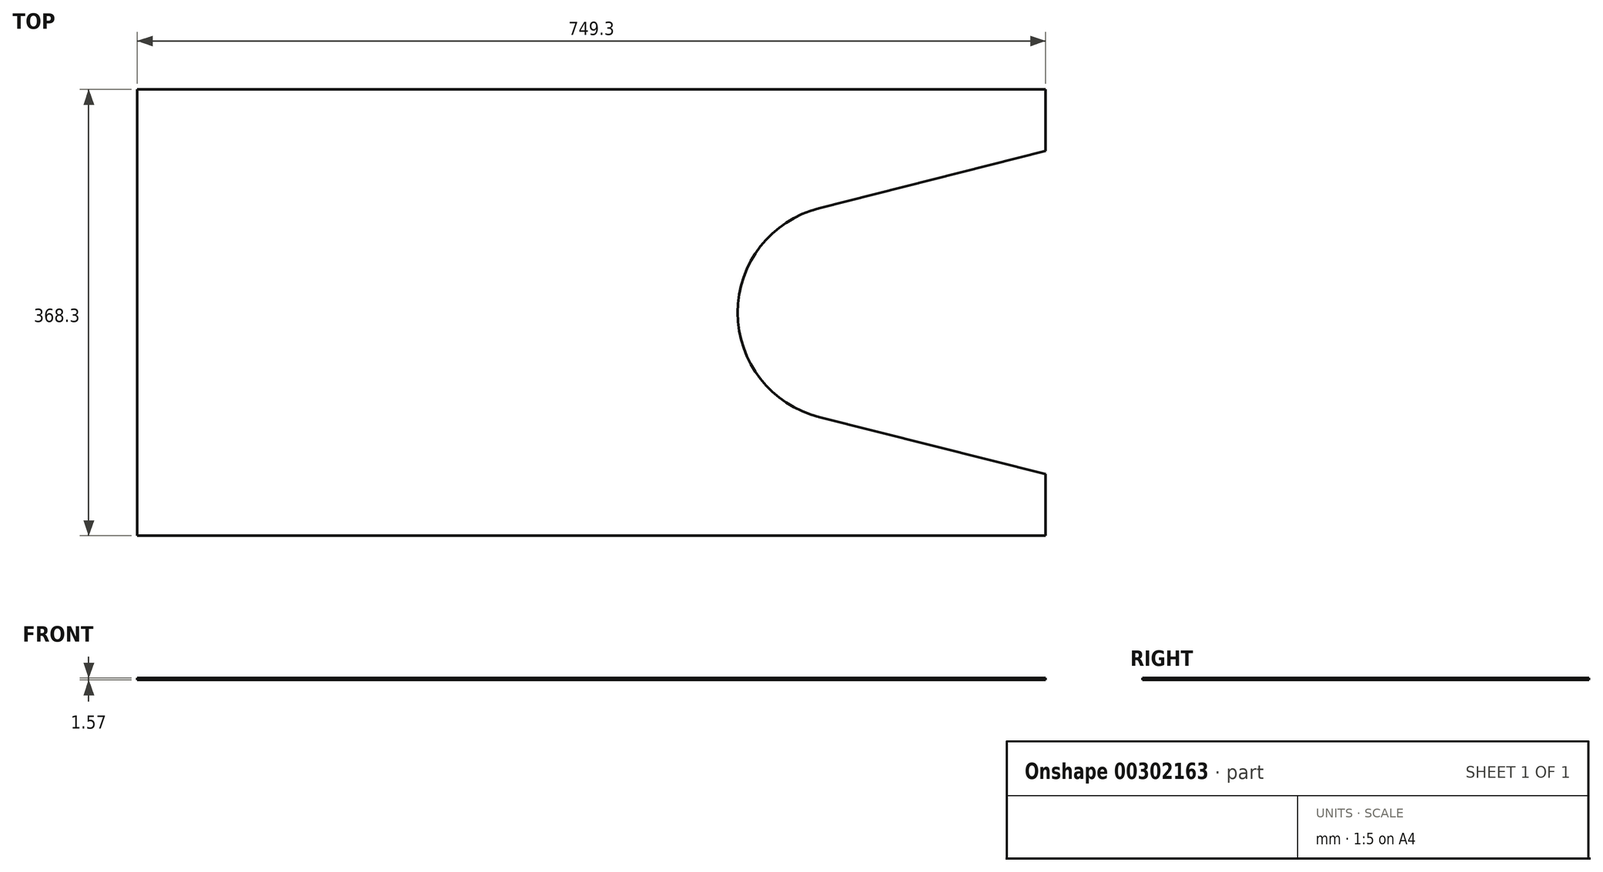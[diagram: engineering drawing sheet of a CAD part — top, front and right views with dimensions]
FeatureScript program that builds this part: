
annotation { "Feature Type Name" : "Feature", "Feature Type Description" : "" }
export const myFeature = defineFeature(function(context is Context, id is Id, definition is map)
    precondition{}
    {
        {
            var Q0;
            Q0=qCreatedBy(makeId("Top.planeOp"),FACE);
            var sketch = newSketch(context, id + "F0", { "sketchPlane" : qUnion([Q0])});
            skLineSegment(sketch, "E0.bottom", {"start": v(0, 0) * mm, "end": v(749.3, 0) * mm});
            skLineSegment(sketch, "E0.top", {"start": v(0, 368.3) * mm, "end": v(749.3, 368.3) * mm});
            skLineSegment(sketch, "E0.left", {"start": v(0, 0) * mm, "end": v(0, 368.3) * mm});
            skLineSegment(sketch, "E0.right", {"start": v(749.3, 0) * mm, "end": v(749.3, 368.3) * mm});
            skPoint(sketch, "E1", {"position": v(749.3, 50.8) * mm});
            skPoint(sketch, "E2", {"position": v(749.3, 317.5) * mm});
            skLineSegment(sketch, "E3", {"start": v(749.3, 184.15) * mm, "end": v(395.05, 184.15) * mm});
            skPoint(sketch, "E3.endSnap0", {"position": v(749.3, 184.15) * mm});
            skPoint(sketch, "E4", {"position": v(495.3, 184.15) * mm});
            skCircle(sketch, "E5", {"center": v(584.2, 184.15) * mm, "radius": 88.9 * mm});
            skLineSegment(sketch, "E6", {"start": v(749.3, 317.5) * mm, "end": v(562.45, 270.35) * mm});
            skLineSegment(sketch, "E7", {"start": v(749.3, 50.8) * mm, "end": v(562.45, 97.95) * mm});
            skSolve(sketch);
        }
        {
            var Q0;
            {var subQ1=sQuery(id+"F0.wireOp",EDGE,"E0.bottom");Q0=makeQuery(id+"F0.imprint","IMPRINT",FACE,{"disambiguationData":[TD([[makeQuery(id+"F0.imprint","IMPRINT",EDGE,{"derivedFrom":subQ1}),1.0]])]});}
            extrude(context, id + "F1", {"entities" : qUnion([Q0]), "depth" : 1.57 * mm});
        }
    });
